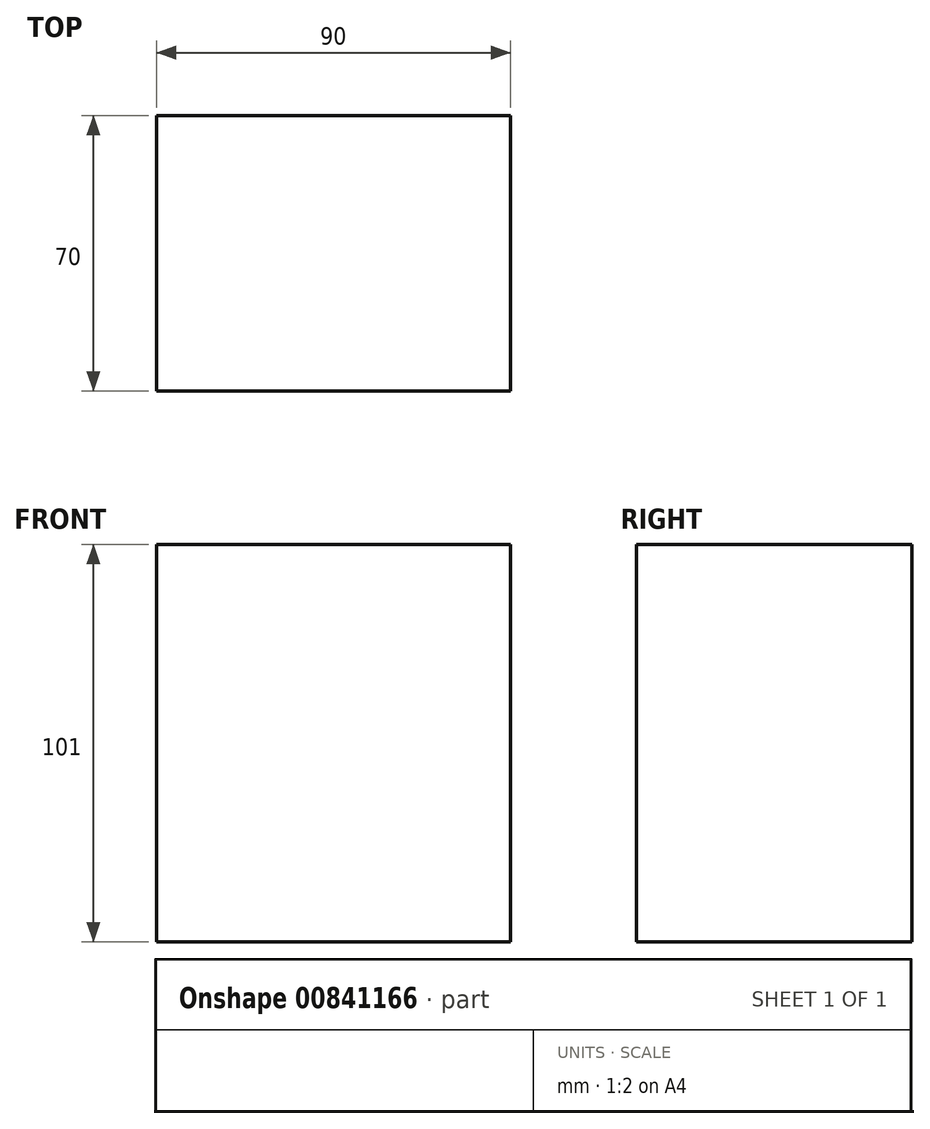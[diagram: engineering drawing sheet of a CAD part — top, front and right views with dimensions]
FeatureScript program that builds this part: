
annotation { "Feature Type Name" : "Feature", "Feature Type Description" : "" }
export const myFeature = defineFeature(function(context is Context, id is Id, definition is map)
    precondition{}
    {
        {
            var Q0;
            Q0=qCreatedBy(makeId("Top.planeOp"),FACE);
            var sketch = newSketch(context, id + "F0", { "sketchPlane" : qUnion([Q0])});
            skLineSegment(sketch, "E0.bottom", {"start": v(45, -35) * mm, "end": v(-45, -35) * mm});
            skLineSegment(sketch, "E0.top", {"start": v(45, 35) * mm, "end": v(-45, 35) * mm});
            skLineSegment(sketch, "E0.left", {"start": v(45, -35) * mm, "end": v(45, 35) * mm});
            skLineSegment(sketch, "E0.right", {"start": v(-45, -35) * mm, "end": v(-45, 35) * mm});
            skPoint(sketch, "E0.middle", {"position": v(0, 0) * mm});
            skSolve(sketch);
        }
        {
            var Q0;
            Q0=makeQuery(id+"F0.imprint","IMPRINT",FACE,{"disambiguationData":[TD([[makeQuery(id+"F0.imprint","IMPRINT",EDGE,{"derivedFrom":sQuery(id+"F0.wireOp",EDGE,"E0.bottom")}),-1.0]])]});
            extrude(context, id + "F1", {"entities" : qUnion([Q0]), "depth" : 101 * mm, "offsetDistance" : 25 * mm});
        }
    });
